FCSTD DOCUMENT  (FreeCAD 0.17R13541 (Git))
Label: screw-temp
License: All rights reserved
LicenseURL: http://en.wikipedia.org/wiki/All_rights_reserved
objects: Sketcher::SketchObject×1, PartDesign::Body×1
note: 2 computed .brp shape members not serialized (recipe doc carries the construction recipe); baked Part::Feature solids carry a one-line shape summary decoded from their .brp

FEATURE [Sketcher::SketchObject] Sketch
  MapMode = 5
  Support = -> [XY_Plane]
  sketch-geometry (6):
    g0: LineSegment StartX=-1.25 StartY=-1.7 StartZ=0 EndX=-2.95 EndY=0 EndZ=0
    g1: LineSegment StartX=-2.95 StartY=0 StartZ=0 EndX=2.95 EndY=0 EndZ=0
    g2: LineSegment StartX=2.95 StartY=0 StartZ=0 EndX=1.25 EndY=-1.7 EndZ=0
    g3: LineSegment StartX=-1.25 StartY=-1.7 StartZ=0 EndX=-1.25 EndY=-6 EndZ=0
    g4: LineSegment StartX=-1.25 StartY=-6 StartZ=0 EndX=1.25 EndY=-6 EndZ=0
    g5: LineSegment StartX=1.25 StartY=-6 StartZ=0 EndX=1.25 EndY=-1.7 EndZ=0
  constraints (18):
    c: Coincident(g1,g2)
    c: Coincident(g0,g1)
    c: Perpendicular(g0,g2)
    c: Horizontal(g1)
    c: Angle(g1,g2) = 0.785398
    c: Coincident(g2,g5)
    c: Coincident(g0,g3)
    c: Coincident(g3,g4)
    c: Coincident(g4,g5)
    c: Horizontal(g2,g0)
    c: Vertical(g5)
    c: Vertical(g3)
    c: Horizontal(g4)
    c: Distance(g1) = 5.9
    c: DistanceY(g2,g1) = 1.7
    c: Distance(g3,g1) = 6
    c: DistanceX(g-2,g1) = 2.95
    c: PointOnObject(g1,g-1)
FEATURE [PartDesign::Body] Body
  Group = -> [Sketch]
  Origin = -> Origin
